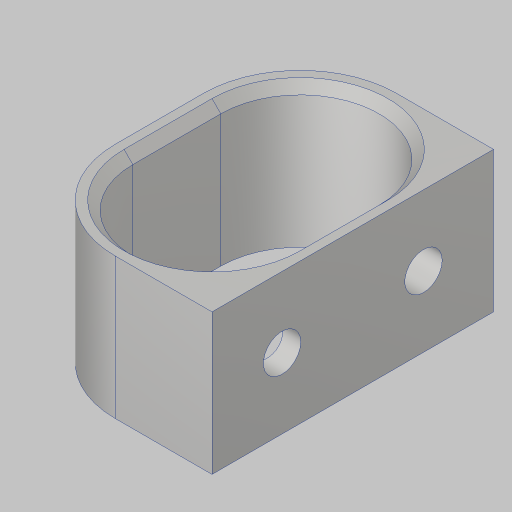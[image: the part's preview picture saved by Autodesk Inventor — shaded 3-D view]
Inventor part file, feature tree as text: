
AUTODESK INVENTOR PART (.ipt)
format: ipt  version: 2023.5 (Build 275446000, 446)  size: 182,272 bytes
history: native  units: in
note: dims shown in document units (in); Inventor stores cm internally (conversion verified against a paired STEP export)
features: projected_geometry x5, extrude x4, sketch x3, chamfer x1
ambient origin geometry x8: Origin, YZ Plane, XZ Plane, XY Plane, X Axis, Y Axis, Z Axis, Center Point
bodies: Solid1 (feature_tree)
feature tree (13):
  sketch  "Sketch1"  dims[d1=1.375in d2=0.125in]
  extrude  "Extrusion1"  Depth=0.125in
  extrude  "Extrusion2"  Depth=1.0in TaperAngle=0.0deg
  extrude  "Extrusion3"  Depth=1.005in
  chamfer  "Chamfer1"  Distance=1.0in
  extrude  "Extrusion4"  Depth=1.0in TaperAngle=0.0deg
  sketch  "Sketch2"  dims[d3=2.0in d4=1.0in d5=0.0in]
  projected_geometry  "Projected Loop1"
  projected_geometry  "Projected Loop2"
  projected_geometry  "Projected Loop3"
  sketch  "Sketch3"  dims[d6=0.2657in d7=1.005in d8=1.0in d9=0.0in d10=1.0in d11=0.0in d12=0.0625in d13=0.125in d14=45.0deg d15=0.25in d16=0.0in]
  projected_geometry  "Projected Loop4"
  projected_geometry  "Projected Loop5"
